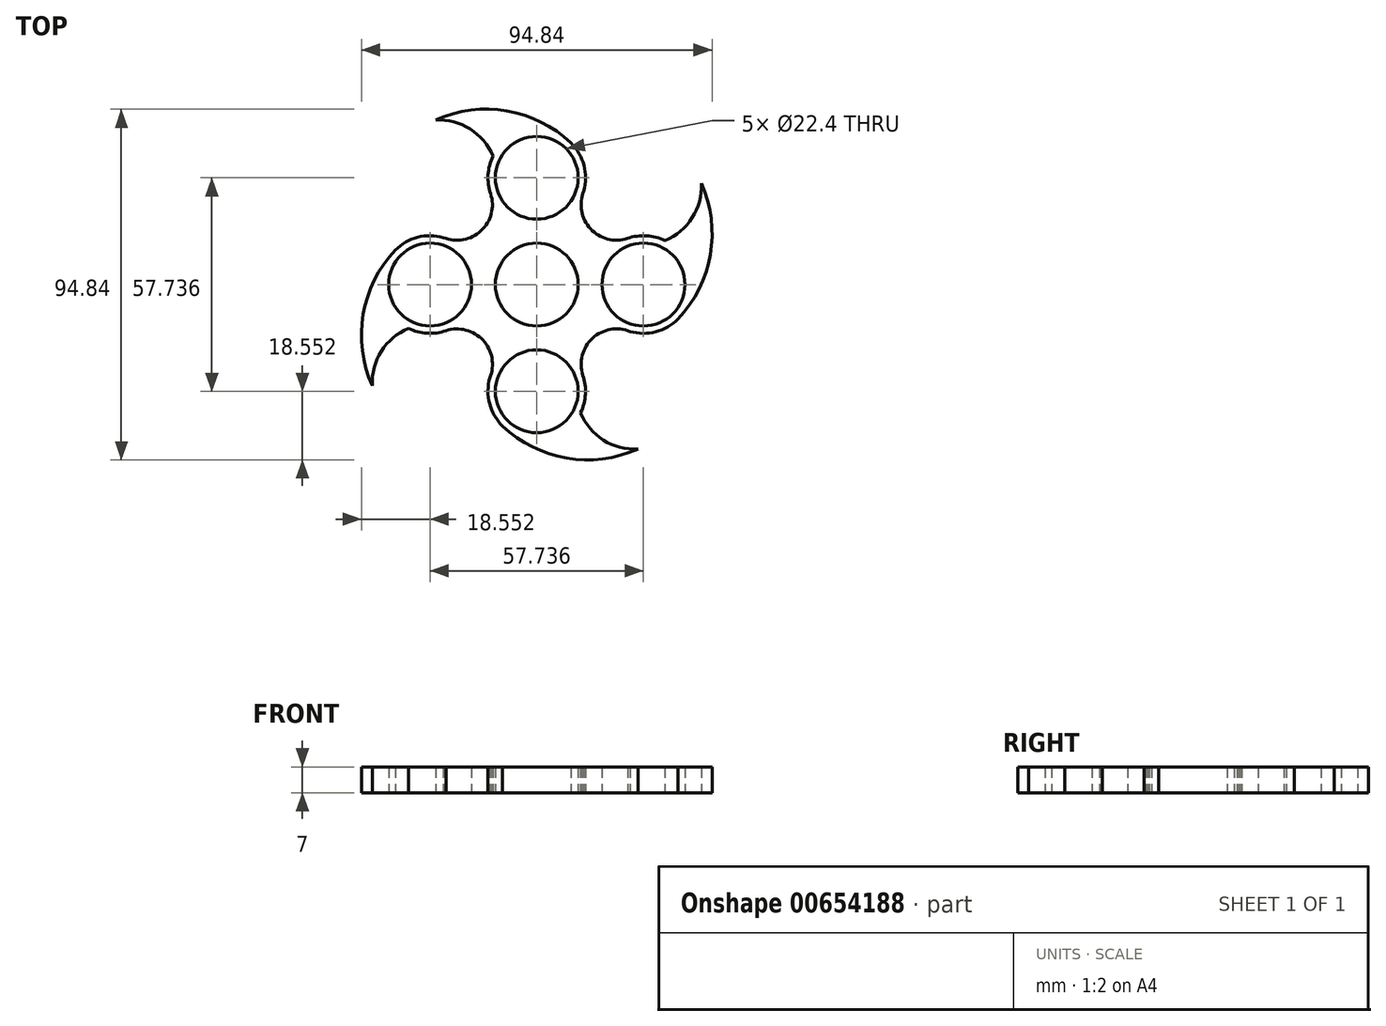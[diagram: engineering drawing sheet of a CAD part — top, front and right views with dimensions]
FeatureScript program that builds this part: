
annotation { "Feature Type Name" : "Feature", "Feature Type Description" : "" }
export const myFeature = defineFeature(function(context is Context, id is Id, definition is map)
    precondition{}
    {
        {
            var Q0;
            Q0=qCreatedBy(makeId("Top.planeOp"),FACE);
            var sketch = newSketch(context, id + "F0", { "sketchPlane" : qUnion([Q0])});
            skCircle(sketch, "E0", {"center": v(0, 0) * mm, "radius": 11.2 * mm});
            skCircle(sketch, "E1", {"center": v(0, 28.87) * mm, "radius": 11.2 * mm});
            skArc(sketch, "E2", {"start": v(12.3, 24.07) * mm, "mid": v(12.8, 32.07) * mm, "end": v(8.6, 38.88) * mm});
            skCircle(sketch, "E3.1.0", {"center": v(-28.87, 0) * mm, "radius": 11.2 * mm});
            skArc(sketch, "E3.1.1", {"start": v(-34.68, -11.85) * mm, "mid": v(-29.68, -13.17) * mm, "end": v(-24.55, -12.47) * mm});
            skCircle(sketch, "E3.2.0", {"center": v(0, -28.87) * mm, "radius": 11.2 * mm});
            skArc(sketch, "E3.2.1", {"start": v(-12.3, -24.07) * mm, "mid": v(-12.8, -32.07) * mm, "end": v(-8.6, -38.88) * mm});
            skCircle(sketch, "E3.3.0", {"center": v(28.87, 0) * mm, "radius": 11.2 * mm});
            skArc(sketch, "E3.3.1", {"start": v(24.07, -12.3) * mm, "mid": v(32.07, -12.8) * mm, "end": v(38.88, -8.6) * mm});
            skArc(sketch, "E4", {"start": v(9.3, 38.24) * mm, "mid": v(-8.09, 46.95) * mm, "end": v(-27.37, 44.5) * mm});
            skArc(sketch, "E5", {"start": v(-11.85, 34.68) * mm, "mid": v(-18.05, 42.06) * mm, "end": v(-27.37, 44.5) * mm});
            skArc(sketch, "E6.1.0", {"start": v(-34.68, -11.85) * mm, "mid": v(-42.06, -18.05) * mm, "end": v(-44.5, -27.37) * mm});
            skArc(sketch, "E6.1.1", {"start": v(-38.24, 9.3) * mm, "mid": v(-46.95, -8.09) * mm, "end": v(-44.5, -27.37) * mm});
            skArc(sketch, "E6.2.0", {"start": v(11.85, -34.68) * mm, "mid": v(18.05, -42.06) * mm, "end": v(27.37, -44.5) * mm});
            skArc(sketch, "E6.2.1", {"start": v(-9.3, -38.24) * mm, "mid": v(8.09, -46.95) * mm, "end": v(27.37, -44.5) * mm});
            skArc(sketch, "E6.3.0", {"start": v(34.68, 11.85) * mm, "mid": v(42.06, 18.05) * mm, "end": v(44.5, 27.37) * mm});
            skArc(sketch, "E6.3.1", {"start": v(38.24, -9.3) * mm, "mid": v(46.95, 8.09) * mm, "end": v(44.5, 27.37) * mm});
            skArc(sketch, "E7", {"start": v(12.7, 25.27) * mm, "mid": v(14.54, 15.08) * mm, "end": v(24.55, 12.47) * mm});
            skArc(sketch, "E8.1.0", {"start": v(-25.27, 12.7) * mm, "mid": v(-15.08, 14.54) * mm, "end": v(-12.47, 24.55) * mm});
            skArc(sketch, "E8.2.0", {"start": v(-12.7, -25.27) * mm, "mid": v(-14.54, -15.08) * mm, "end": v(-24.55, -12.47) * mm});
            skArc(sketch, "E8.3.0", {"start": v(25.27, -12.7) * mm, "mid": v(15.08, -14.54) * mm, "end": v(12.47, -24.55) * mm});
            skArc(sketch, "E9.trimOffspring", {"start": v(-11.85, 34.68) * mm, "mid": v(-13.17, 29.68) * mm, "end": v(-12.47, 24.55) * mm});
            skArc(sketch, "E10.trimOffspring", {"start": v(-24.07, 12.3) * mm, "mid": v(-32.07, 12.8) * mm, "end": v(-38.88, 8.6) * mm});
            skArc(sketch, "E11.trimOffspring", {"start": v(11.85, -34.68) * mm, "mid": v(13.17, -29.68) * mm, "end": v(12.47, -24.55) * mm});
            skArc(sketch, "E12.trimOffspring", {"start": v(34.68, 11.85) * mm, "mid": v(29.68, 13.17) * mm, "end": v(24.55, 12.47) * mm});
            skSolve(sketch);
        }
        {
            var Q0;
            Q0=makeQuery(id+"F0.imprint","IMPRINT",FACE,{"disambiguationData":[TD([[makeQuery(id+"F0.imprint","IMPRINT",EDGE,{"derivedFrom":sQuery(id+"F0.wireOp",EDGE,"E0")}),-1.0]])]});
            extrude(context, id + "F1", {"entities" : qUnion([Q0]), "depth" : 7 * mm, "offsetDistance" : 25 * mm});
        }
    });
